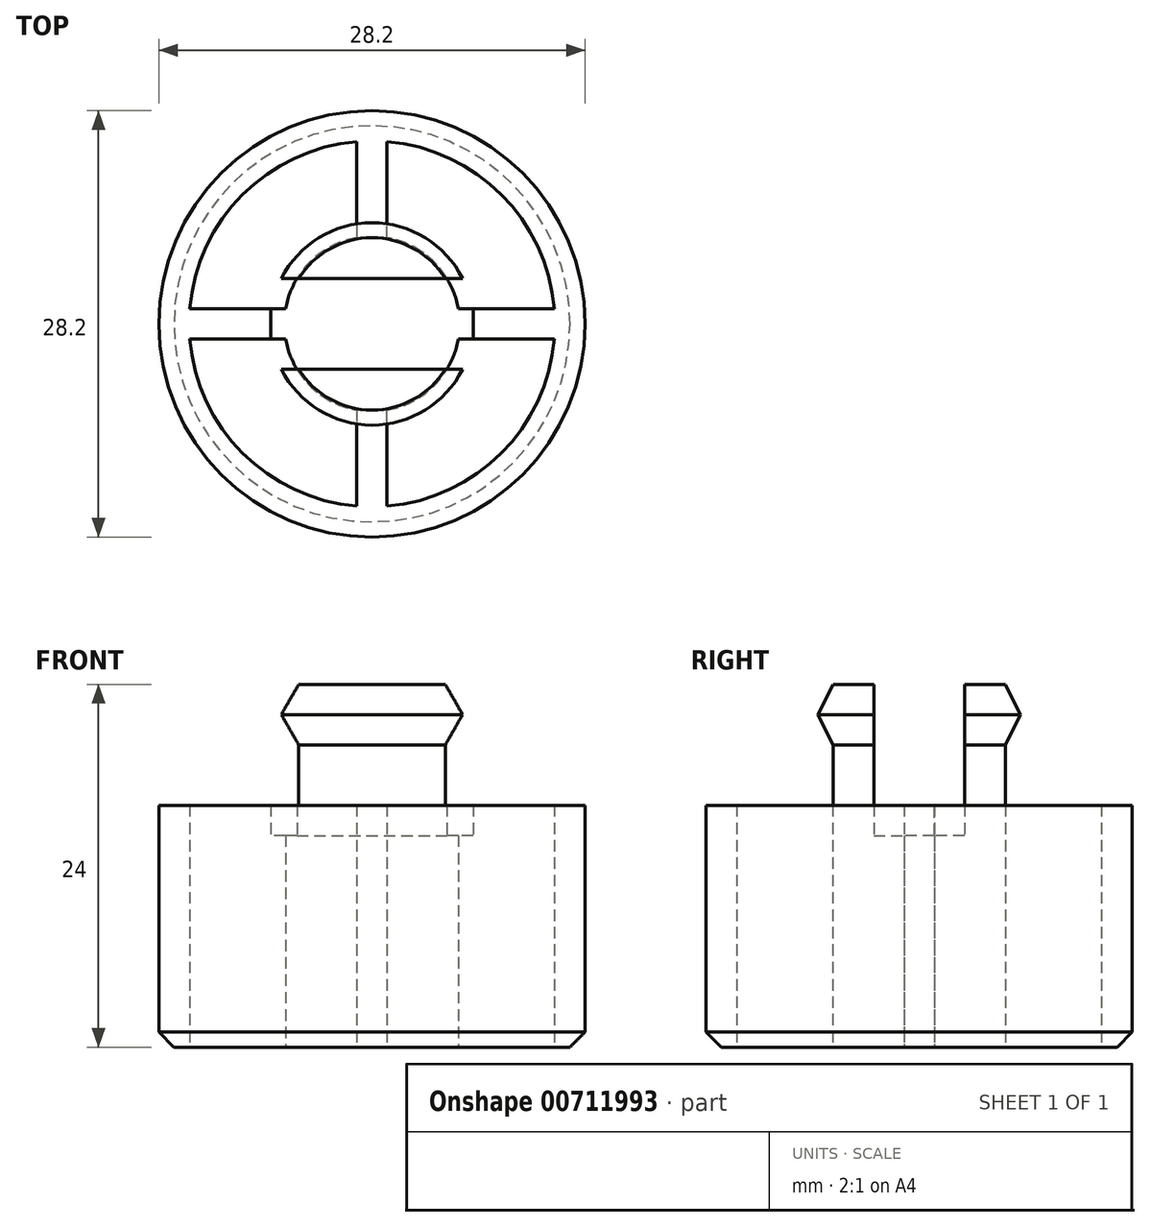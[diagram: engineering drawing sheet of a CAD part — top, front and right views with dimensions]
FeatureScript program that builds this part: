
annotation { "Feature Type Name" : "Feature", "Feature Type Description" : "" }
export const myFeature = defineFeature(function(context is Context, id is Id, definition is map)
    precondition{}
    {
        {
            var Q0;
            Q0=qCreatedBy(makeId("Top.planeOp"),FACE);
            var sketch = newSketch(context, id + "F0", { "sketchPlane" : qUnion([Q0])});
            skCircle(sketch, "E0", {"center": v(0, 0) * mm, "radius": 14.1 * mm});
            skArc(sketch, "E1", {"start": v(-1, 12.06) * mm, "mid": v(-8.56, 8.56) * mm, "end": v(-12.06, 1) * mm});
            skArc(sketch, "E2", {"start": v(-1, 5.71) * mm, "mid": v(-4.1, 4.1) * mm, "end": v(-5.71, 1) * mm});
            skLineSegment(sketch, "E3", {"start": v(-1, 12.06) * mm, "end": v(-1, 5.71) * mm});
            skLineSegment(sketch, "E4", {"start": v(1, -12.06) * mm, "end": v(1, -5.71) * mm});
            skLineSegment(sketch, "E5", {"start": v(-12.06, 1) * mm, "end": v(-5.71, 1) * mm});
            skLineSegment(sketch, "E6", {"start": v(12.06, -1) * mm, "end": v(5.71, -1) * mm});
            skArc(sketch, "E7.trimOffspring", {"start": v(-5.71, -1) * mm, "mid": v(-4.1, -4.1) * mm, "end": v(-1, -5.71) * mm});
            skLineSegment(sketch, "E8.trimOffspring", {"start": v(5.71, 1) * mm, "end": v(12.06, 1) * mm});
            skLineSegment(sketch, "E9.trimOffspring", {"start": v(-1, -5.71) * mm, "end": v(-1, -12.06) * mm});
            skLineSegment(sketch, "E10.trimOffspring", {"start": v(1, 5.71) * mm, "end": v(1, 12.06) * mm});
            skLineSegment(sketch, "E11.trimOffspring", {"start": v(-5.71, -1) * mm, "end": v(-12.06, -1) * mm});
            skArc(sketch, "E12.trimOffspring", {"start": v(5.71, 1) * mm, "mid": v(4.1, 4.1) * mm, "end": v(1, 5.71) * mm});
            skArc(sketch, "E13.trimOffspring", {"start": v(1, -5.71) * mm, "mid": v(4.1, -4.1) * mm, "end": v(5.71, -1) * mm});
            skArc(sketch, "E14.trimOffspring", {"start": v(1, -12.06) * mm, "mid": v(8.56, -8.56) * mm, "end": v(12.06, -1) * mm});
            skArc(sketch, "E15.trimOffspring", {"start": v(12.06, 1) * mm, "mid": v(8.56, 8.56) * mm, "end": v(1, 12.06) * mm});
            skArc(sketch, "E16.trimOffspring", {"start": v(-12.06, -1) * mm, "mid": v(-8.56, -8.56) * mm, "end": v(-1, -12.06) * mm});
            skSolve(sketch);
        }
        {
            var Q0;
            Q0 = qSketchRegion(id + "F0", true);
            extrude(context, id + "F1", {"entities" : qUnion([Q0]), "depth" : 16 * mm, "offsetDistance" : 25 * mm});
        }
        {
            var Q0;
            Q0=makeQuery(id+"F1.opExtrude","CAP_EDGE",EDGE,{"disambiguationData":[OSD([sQuery(id+"F0.wireOp",EDGE,"E0")])],"isStart":true});
            chamfer(context, id + "F2", {"entities" : qUnion([Q0]), "width" : 1 * mm, "tangentPropagation" : true});
        }
        {
            var Q0;
            Q0=makeQuery(id+"F1.opExtrude","CAP_FACE",FACE,{"disambiguationData":[OSD([sQuery(id+"F0.wireOp",EDGE,"E0"),sQuery(id+"F0.wireOp",EDGE,"E1"),sQuery(id+"F0.wireOp",EDGE,"E2"),sQuery(id+"F0.wireOp",EDGE,"E3"),sQuery(id+"F0.wireOp",EDGE,"E4"),sQuery(id+"F0.wireOp",EDGE,"E5"),sQuery(id+"F0.wireOp",EDGE,"E6"),sQuery(id+"F0.wireOp",EDGE,"E7.trimOffspring"),sQuery(id+"F0.wireOp",EDGE,"E8.trimOffspring"),sQuery(id+"F0.wireOp",EDGE,"E9.trimOffspring"),sQuery(id+"F0.wireOp",EDGE,"E10.trimOffspring"),sQuery(id+"F0.wireOp",EDGE,"E11.trimOffspring"),sQuery(id+"F0.wireOp",EDGE,"E12.trimOffspring"),sQuery(id+"F0.wireOp",EDGE,"E13.trimOffspring"),sQuery(id+"F0.wireOp",EDGE,"E14.trimOffspring"),sQuery(id+"F0.wireOp",EDGE,"E15.trimOffspring"),sQuery(id+"F0.wireOp",EDGE,"E16.trimOffspring")])],"isStart":false});
            var sketch = newSketch(context, id + "F3", { "sketchPlane" : qUnion([Q0])});
            skCircle(sketch, "E17", {"center": v(0, 0) * mm, "radius": 5.7 * mm});
            skSolve(sketch);
        }
        {
            var Q0;
            Q0 = qSketchRegion(id + "F3", true);
            extrude(context, id + "F4", {"entities" : qUnion([Q0]), "operationType" : NewBodyOperationType.ADD, "depth" : 8 * mm, "offsetDistance" : 25 * mm});
        }
        {
            var Q0;
            Q0=makeQuery(id+"F4.opExtrude","CAP_FACE",FACE,{"disambiguationData":[OSD([sQuery(id+"F3.wireOp",EDGE,"E17")])],"isStart":false});
            var sketch = newSketch(context, id + "F5", { "sketchPlane" : qUnion([Q0])});
            skCircle(sketch, "E18", {"center": v(0, 0) * mm, "radius": 6.7 * mm});
            skCircle(sketch, "E19", {"center": v(0, 0) * mm, "radius": 5.7 * mm});
            skSolve(sketch);
        }
        {
            var Q0;
            Q0 = qSketchRegion(id + "F5", true);
            extrude(context, id + "F6", {"entities" : qUnion([Q0]), "operationType" : NewBodyOperationType.ADD, "oppositeDirection" : true, "depth" : 4 * mm, "offsetDistance" : 25 * mm});
        }
        {
            var Q0;
            Q0=makeQuery(id+"F6.opExtrude","CAP_EDGE",EDGE,{"disambiguationData":[OSD([sQuery(id+"F5.wireOp",EDGE,"E18")])],"isStart":true});
            var Q1;
            Q1=makeQuery(id+"F6.opExtrude","CAP_EDGE",EDGE,{"disambiguationData":[OSD([sQuery(id+"F5.wireOp",EDGE,"E18")])],"isStart":false});
            chamfer(context, id + "F7", {"entities" : qUnion([Q0, Q1]), "chamferType" : ChamferType.TWO_OFFSETS, "width1" : 1 * mm, "oppositeDirection" : false, "width2" : 2 * mm, "tangentPropagation" : true});
        }
        {
            var Q0;
            Q0=makeQuery(id+"F6.boolean.opBoolean","MERGE",FACE,{"derivedFrom":[makeQuery(id+"F4.opExtrude","CAP_FACE",FACE,{"disambiguationData":[OSD([sQuery(id+"F3.wireOp",EDGE,"E17")])],"isStart":false}),makeQuery(id+"F6.opExtrude","CAP_FACE",FACE,{"disambiguationData":[OSD([sQuery(id+"F5.wireOp",EDGE,"E18"),sQuery(id+"F5.wireOp",EDGE,"E19")])],"isStart":true})]});
            var sketch = newSketch(context, id + "F8", { "sketchPlane" : qUnion([Q0])});
            skLineSegment(sketch, "E20.bottom", {"start": v(-6.7, 3) * mm, "end": v(6.7, 3) * mm});
            skLineSegment(sketch, "E20.top", {"start": v(-6.7, -3) * mm, "end": v(6.7, -3) * mm});
            skLineSegment(sketch, "E20.left", {"start": v(-6.7, 3) * mm, "end": v(-6.7, -3) * mm});
            skLineSegment(sketch, "E20.right", {"start": v(6.7, 3) * mm, "end": v(6.7, -3) * mm});
            skPoint(sketch, "E20.middle", {"position": v(0, 0) * mm});
            skSolve(sketch);
        }
        {
            var Q0;
            Q0 = qSketchRegion(id + "F8", true);
            extrude(context, id + "F9", {"entities" : qUnion([Q0]), "operationType" : NewBodyOperationType.REMOVE, "oppositeDirection" : true, "depth" : 10 * mm, "offsetDistance" : 25 * mm});
        }
    });
